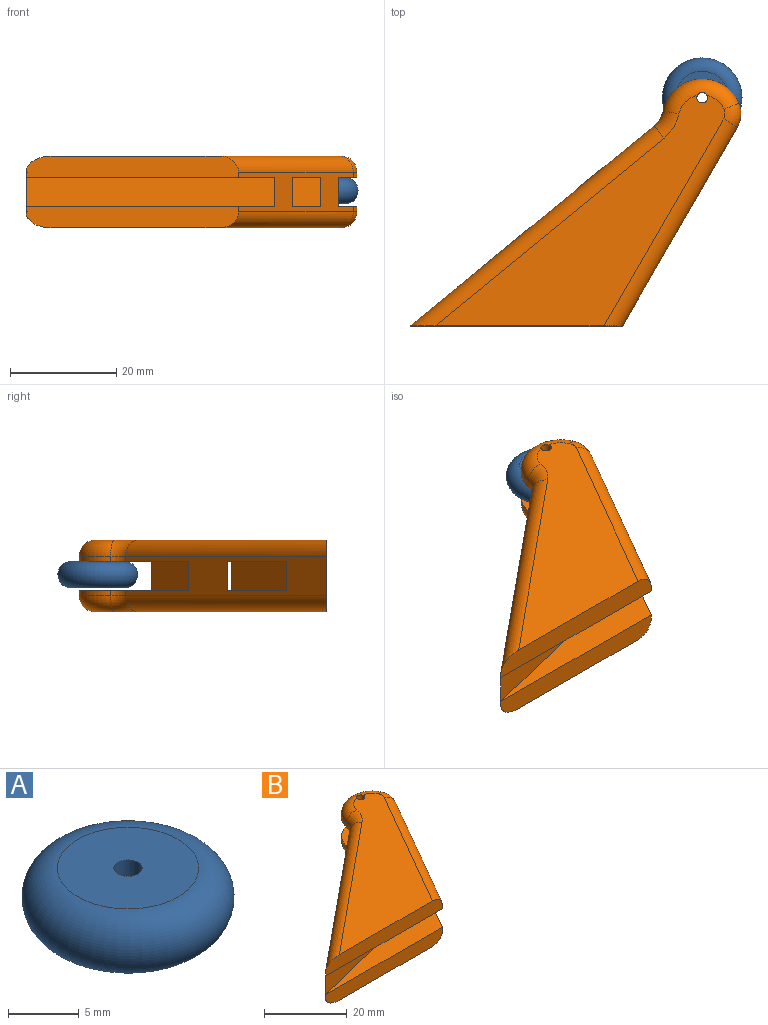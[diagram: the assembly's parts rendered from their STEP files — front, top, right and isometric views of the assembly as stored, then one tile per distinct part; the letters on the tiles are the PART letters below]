
ASSEMBLY  parts=2 mates=1
PART A: 4 faces, bbox 16.2x16.2x5 mm
  f0: cylinder r=1mm len=5mm, axis (0,0,-1), area 31.4mm2, adj f1,f2
  f1: plane 10x10mm, normal (0,0,1), area 75.4mm2, adj f0,f3
  f2: plane 10x10mm, normal (0,0,-1), area 75.4mm2, adj f0,f3
  f3: torus R=5mm, axis (0,0,1), area 325.3mm2, adj f1,f2
PART B: 34 faces, bbox 62.5x49.4x13.5 mm
  f0: plane 46.75x11.69mm, normal (0,0,1), area 233.7mm2, adj f3,f4,f26
  f1: plane 30.67x20.53mm, normal (0,0,1), area 255.3mm2, adj f2,f4,f5,f6,f7,f8,f27
  f2: plane 45.94x37.69mm, normal (-0.63,0.77,0), area 247.4mm2, adj f1,f3,f7,f9,f15,f16,f18,f21
  f3: plane 40x4mm, normal (0,-1,0), area 154.7mm2, adj f0,f2,f4,f10,f11,f15
  f4: plane 37.46x21.63mm, normal (0.87,-0.5,0), area 163mm2, adj f0,f1,f3,f5,f9,f11,f16,f17
  f5: cylinder r=5mm len=4.48mm, axis (0,0,-1), area 4.6mm2, adj f1,f4,f6,f12
  f6: cylinder r=7.5mm len=14.23mm, axis (0,0,-1), area 19mm2, adj f1,f5,f7,f13
  f7: cylinder r=5mm len=2.83mm, axis (0,0,-1), area 3.4mm2, adj f1,f2,f6,f14
  f8: cylinder r=1mm len=4mm, axis (0,0,-1), area 25.1mm2, adj f1,f10,f13
  f9: plane 46.41x19.33mm, normal (0,0,1), area 286.2mm2, adj f2,f4,f25,f28
  f10: plane 54.57x43.38mm, normal (0,0,-1), area 784mm2, adj f3,f8,f11,f12,f13,f14,f15
  f11: cylinder r=3mm len=40.46mm, axis (0.5,0.87,0), area 206.8mm2, adj f3,f4,f10,f12
  f12: torus R=2mm, axis (0,0,1), area 17.1mm2, adj f5,f10,f11,f13
  f13: torus R=4.5mm, axis (0,0,1), area 75.7mm2, adj f6,f8,f10,f12,f14
  f14: torus R=8mm, axis (0,0,1), area 19.4mm2, adj f7,f10,f13,f15
  f15: cylinder r=3mm len=47.85mm, axis (-0.77,-0.63,0), area 273.8mm2, adj f2,f3,f10,f14
  f16: plane 30.67x20.53mm, normal (0,0,-1), area 255.3mm2, adj f2,f4,f19,f20,f21,f22,f27
  f17: plane 46.75x11.69mm, normal (0,0,-1), area 233.7mm2, adj f4,f18,f26
  f18: plane 40x4mm, normal (0,-1,0), area 154.7mm2, adj f2,f4,f17,f23,f29,f33
  f19: cylinder r=5mm len=4.48mm, axis (0,0,-1), area 4.6mm2, adj f4,f16,f20,f32
  f20: cylinder r=7.5mm len=14.23mm, axis (0,0,-1), area 19mm2, adj f16,f19,f21,f31
  f21: cylinder r=5mm len=2.83mm, axis (0,0,-1), area 3.4mm2, adj f2,f16,f20,f30
  f22: cylinder r=1mm len=4mm, axis (0,0,-1), area 25.1mm2, adj f16,f23,f31
  f23: plane 54.57x43.38mm, normal (0,0,1), area 784mm2, adj f18,f22,f29,f30,f31,f32,f33
  f24: plane 46.41x19.33mm, normal (0,0,-1), area 286.2mm2, adj f2,f4,f25,f28
  f25: plane 41.19x10.3mm, normal (-0.24,0.97,0), area 233.5mm2, adj f2,f4,f9,f24
  f26: plane 46.75x11.69mm, normal (0.24,-0.97,0), area 265mm2, adj f0,f2,f4,f17
  f27: plane 27.3x6.82mm, normal (-0.24,0.97,0), area 154.8mm2, adj f1,f2,f4,f16
  f28: plane 32.85x8.21mm, normal (0.24,-0.97,0), area 186.3mm2, adj f2,f4,f9,f24
  f29: cylinder r=3mm len=47.85mm, axis (0.77,0.63,0), area 273.8mm2, adj f2,f18,f23,f30
  f30: torus R=8mm, axis (0,0,1), area 19.4mm2, adj f21,f23,f29,f31
  f31: torus R=4.5mm, axis (0,0,1), area 75.7mm2, adj f20,f22,f23,f30,f32
  f32: torus R=2mm, axis (0,0,1), area 17.1mm2, adj f19,f23,f31,f33
  f33: cylinder r=3mm len=40.46mm, axis (-0.5,-0.87,0), area 206.8mm2, adj f4,f18,f23,f32
PLACE A t=(11.42,-24.99,2.75)mm
PLACE B t=(-15.13,-10.37,-1.75)mm
MATE revolute A.f0 <-> B.f8  axis (0,0,1) through (39.87,32.6,7.75)mm
